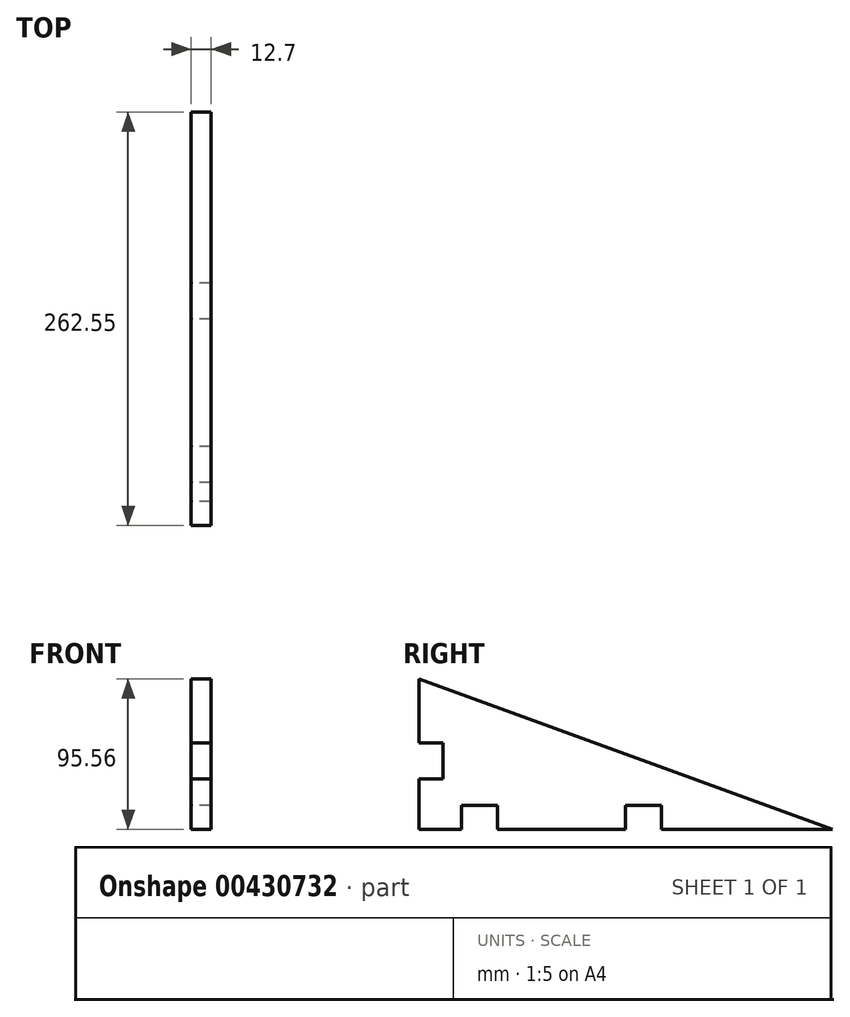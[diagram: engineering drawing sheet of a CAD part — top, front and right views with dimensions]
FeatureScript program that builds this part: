
annotation { "Feature Type Name" : "Feature", "Feature Type Description" : "" }
export const myFeature = defineFeature(function(context is Context, id is Id, definition is map)
    precondition{}
    {
        {
            var Q0;
            Q0=qCreatedBy(makeId("Right.planeOp"),FACE);
            var sketch = newSketch(context, id + "F0", { "sketchPlane" : qUnion([Q0])});
            skLineSegment(sketch, "E0", {"start": v(0, 0) * mm, "end": v(0, 95.56) * mm});
            skLineSegment(sketch, "E1", {"start": v(0, 95.56) * mm, "end": v(262.55, 0) * mm});
            skLineSegment(sketch, "E2", {"start": v(0, 0) * mm, "end": v(262.55, 0) * mm});
            skLineSegment(sketch, "E3.bottom", {"start": v(27.18, 0) * mm, "end": v(50.04, 0) * mm});
            skLineSegment(sketch, "E3.top", {"start": v(27.18, 15.24) * mm, "end": v(50.04, 15.24) * mm});
            skLineSegment(sketch, "E3.left", {"start": v(27.18, 0) * mm, "end": v(27.18, 15.24) * mm});
            skLineSegment(sketch, "E3.right", {"start": v(50.04, 0) * mm, "end": v(50.04, 15.24) * mm});
            skLineSegment(sketch, "E4.bottom", {"start": v(131.28, 0) * mm, "end": v(154.14, 0) * mm});
            skLineSegment(sketch, "E4.top", {"start": v(131.28, 15.24) * mm, "end": v(154.14, 15.24) * mm});
            skLineSegment(sketch, "E4.left", {"start": v(131.28, 0) * mm, "end": v(131.28, 15.24) * mm});
            skLineSegment(sketch, "E4.right", {"start": v(154.14, 0) * mm, "end": v(154.14, 15.24) * mm});
            skLineSegment(sketch, "E5.bottom", {"start": v(0, 54.96) * mm, "end": v(15.24, 54.96) * mm});
            skLineSegment(sketch, "E5.top", {"start": v(0, 32.1) * mm, "end": v(15.24, 32.1) * mm});
            skLineSegment(sketch, "E5.left", {"start": v(0, 54.96) * mm, "end": v(0, 32.1) * mm});
            skLineSegment(sketch, "E5.right", {"start": v(15.24, 54.96) * mm, "end": v(15.24, 32.1) * mm});
            skSolve(sketch);
        }
        {
            var Q0;
            {var subQ3=sQuery(id+"F0.wireOp",EDGE,"E1");Q0=makeQuery(id+"F0.imprint","IMPRINT",FACE,{"disambiguationData":[TD([[makeQuery(id+"F0.imprint","IMPRINT",EDGE,{"derivedFrom":subQ3}),-1.0]])]});}
            extrude(context, id + "F1", {"entities" : qUnion([Q0]), "depth" : 12.7 * mm});
        }
    });
